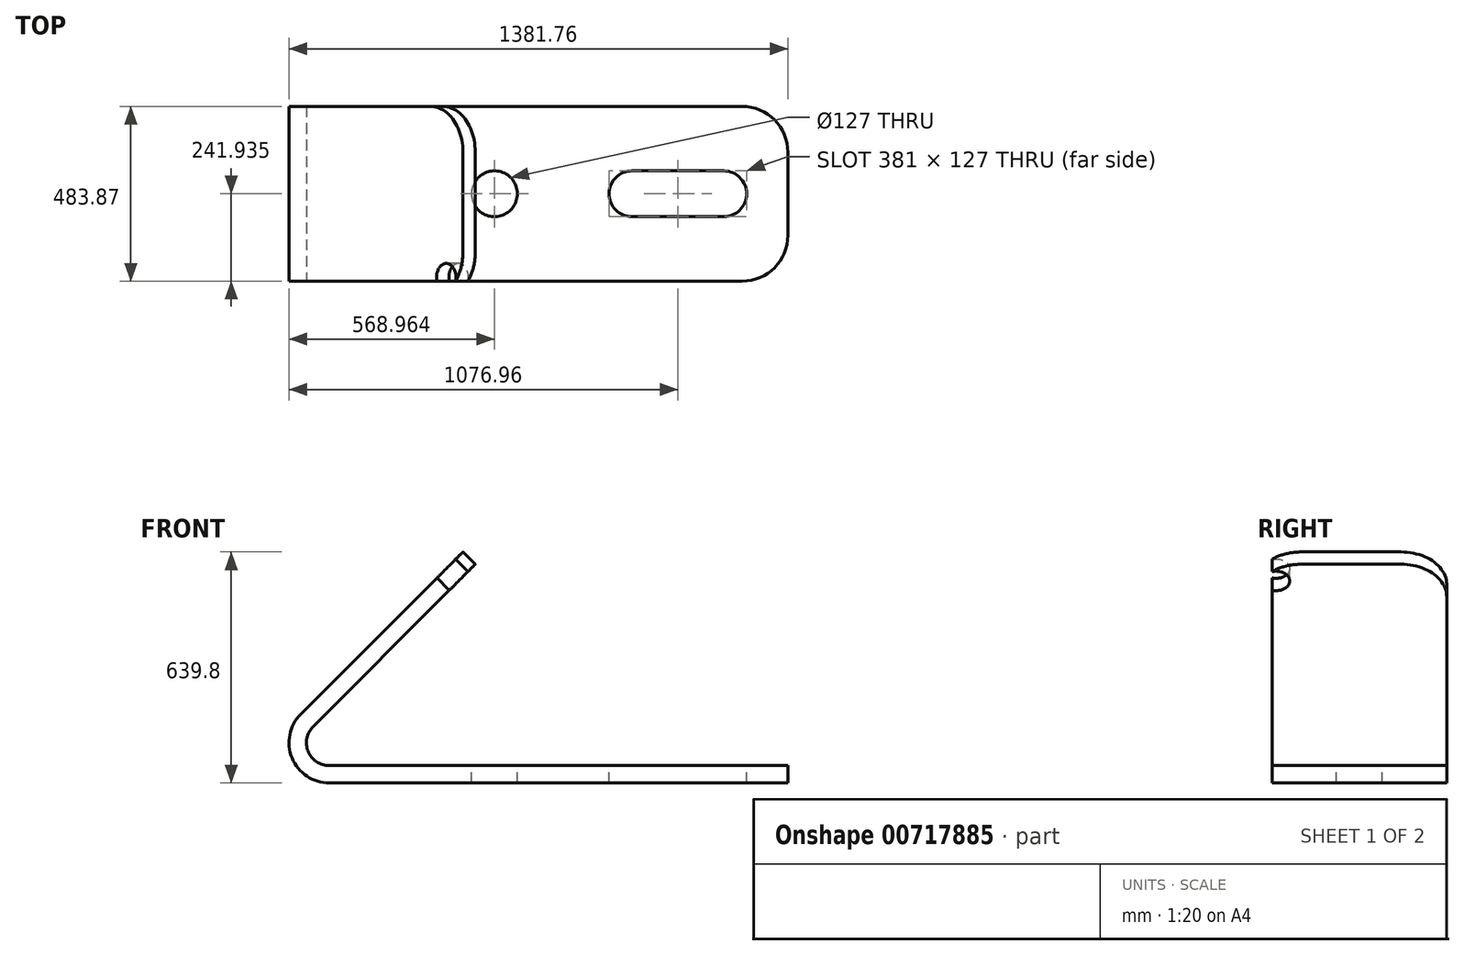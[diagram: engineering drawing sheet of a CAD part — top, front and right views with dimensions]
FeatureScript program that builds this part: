
annotation { "Feature Type Name" : "Feature", "Feature Type Description" : "" }
export const myFeature = defineFeature(function(context is Context, id is Id, definition is map)
    precondition{}
    {
        {
            var Q0;
            Q0=qCreatedBy(makeId("Front.planeOp"),FACE);
            var sketch = newSketch(context, id + "F0", { "sketchPlane" : qUnion([Q0])});
            skLineSegment(sketch, "E0", {"start": v(-755.86, 0) * mm, "end": v(514.14, 0) * mm});
            skLineSegment(sketch, "E1", {"start": v(514.14, 48.26) * mm, "end": v(-755.86, 48.26) * mm});
            skLineSegment(sketch, "E2", {"start": v(514.14, 48.26) * mm, "end": v(514.14, 0) * mm});
            skArc(sketch, "E3", {"start": v(-834.88, 190.79) * mm, "mid": v(-859.1, 69) * mm, "end": v(-755.86, 0) * mm});
            skCircle(sketch, "E4", {"center": v(-755.86, 111.76) * mm, "radius": 63.5 * mm});
            skLineSegment(sketch, "E5", {"start": v(-834.88, 190.79) * mm, "end": v(-385.87, 639.8) * mm});
            skLineSegment(sketch, "E6", {"start": v(-385.87, 639.8) * mm, "end": v(-351.74, 605.67) * mm});
            skLineSegment(sketch, "E7", {"start": v(-351.74, 605.67) * mm, "end": v(-800.76, 156.66) * mm});
            skSolve(sketch);
        }
        {
            var Q0;
            Q0=makeQuery(id+"F0.imprint","IMPRINT",FACE,{"disambiguationData":[TD([[makeQuery(id+"F0.imprint","IMPRINT",EDGE,{"derivedFrom":sQuery(id+"F0.wireOp",EDGE,"E0")}),1.0]])]});
            extrude(context, id + "F1", {"entities" : qUnion([Q0]), "oppositeDirection" : true, "depth" : 483.87 * mm, "offsetDistance" : 25.4 * mm});
        }
        {
            var Q0;
            Q0=makeQuery(id+"F1.opExtrude","SWEPT_FACE",FACE,{"disambiguationData":[OSD([sQuery(id+"F0.wireOp",EDGE,"E1")])]});
            var sketch = newSketch(context, id + "F2", { "sketchPlane" : qUnion([Q0])});
            skLineSegment(sketch, "E8", {"start": v(514.14, 483.87) * mm, "end": v(-298.66, 483.87) * mm, "construction": true});
            skLineSegment(sketch, "E9", {"start": v(-298.66, 483.87) * mm, "end": v(-298.66, 241.94) * mm, "construction": true});
            skCircle(sketch, "E10", {"center": v(-298.66, 241.94) * mm, "radius": 63.5 * mm});
            skLineSegment(sketch, "E11", {"start": v(18.84, 241.94) * mm, "end": v(399.84, 241.94) * mm, "construction": true});
            skLineSegment(sketch, "E12", {"start": v(82.34, 305.44) * mm, "end": v(336.34, 305.44) * mm});
            skLineSegment(sketch, "E13.MirrorCS", {"start": v(82.34, 178.44) * mm, "end": v(336.34, 178.44) * mm});
            skArc(sketch, "E14", {"start": v(82.34, 305.44) * mm, "mid": v(18.84, 241.93) * mm, "end": v(82.34, 178.43) * mm});
            skArc(sketch, "E15", {"start": v(336.34, 178.44) * mm, "mid": v(399.84, 241.94) * mm, "end": v(336.34, 305.44) * mm});
            skPoint(sketch, "E16.MirrorCS.end.orphan", {"position": v(399.84, 241.94) * mm});
            skPoint(sketch, "E16.MirrorCS.start.orphan", {"position": v(399.84, 178.44) * mm});
            skPoint(sketch, "E17.MirrorCS.end.orphan", {"position": v(18.84, 178.44) * mm});
            skPoint(sketch, "E17.MirrorCS.start.orphan", {"position": v(18.84, 241.94) * mm});
            skSolve(sketch);
        }
        {
            var Q0;
            Q0=makeQuery(id+"F2.imprint","IMPRINT",FACE,{"disambiguationData":[TD([[makeQuery(id+"F2.imprint","IMPRINT",EDGE,{"derivedFrom":sQuery(id+"F2.wireOp",EDGE,"E12")}),-1.0]])]});
            var Q1;
            Q1=makeQuery(id+"F2.imprint","IMPRINT",FACE,{"disambiguationData":[TD([[makeQuery(id+"F2.imprint","IMPRINT",EDGE,{"derivedFrom":sQuery(id+"F2.wireOp",EDGE,"E10")}),1.0]])]});
            extrude(context, id + "F3", {"entities" : qUnion([Q0, Q1]), "operationType" : NewBodyOperationType.REMOVE, "oppositeDirection" : true, "depth" : 83.82 * mm, "offsetDistance" : 25.4 * mm});
        }
        {
            var Q0;
            Q0=makeQuery(id+"F1.opExtrude","SWEPT_FACE",FACE,{"disambiguationData":[OSD([sQuery(id+"F0.wireOp",EDGE,"E5")])]});
            var sketch = newSketch(context, id + "F4", { "sketchPlane" : qUnion([Q0])});
            skLineSegment(sketch, "E18", {"start": v(179.56, 0) * mm, "end": v(-10.94, 0) * mm, "construction": true});
            skLineSegment(sketch, "E19", {"start": v(-10.94, 0) * mm, "end": v(-10.94, 114.3) * mm, "construction": true});
            skCircle(sketch, "E20", {"center": v(-10.94, 114.3) * mm, "radius": 38.1 * mm});
            skLineSegment(sketch, "E21", {"start": v(179.56, 241.94) * mm, "end": v(-455.44, 241.94) * mm, "construction": true});
            skCircle(sketch, "E22.MirrorC", {"center": v(-10.94, 369.57) * mm, "radius": 38.1 * mm});
            skSolve(sketch);
        }
        {
            var Q0;
            Q0=makeQuery(id+"F4.imprint","IMPRINT",FACE,{"disambiguationData":[TD([[makeQuery(id+"F4.imprint","IMPRINT",EDGE,{"derivedFrom":sQuery(id+"F4.wireOp",EDGE,"E22.MirrorC")}),-1.0]])]});
            var Q1;
            Q1=makeQuery(id+"F4.imprint","IMPRINT",FACE,{"disambiguationData":[TD([[makeQuery(id+"F4.imprint","IMPRINT",EDGE,{"derivedFrom":sQuery(id+"F4.wireOp",EDGE,"E20")}),1.0]])]});
            extrude(context, id + "F5", {"entities" : qUnion([Q0, Q1]), "operationType" : NewBodyOperationType.REMOVE, "oppositeDirection" : true, "depth" : 101.6 * mm, "offsetDistance" : 25.4 * mm});
        }
        {
            var Q0;
            Q0=makeQuery(id+"F1.opExtrude","CAP_EDGE",EDGE,{"disambiguationData":[OSD([sQuery(id+"F0.wireOp",EDGE,"E6")])],"isStart":false});
            var Q1;
            Q1=makeQuery(id+"F1.opExtrude","CAP_EDGE",EDGE,{"disambiguationData":[OSD([sQuery(id+"F0.wireOp",EDGE,"E6")])],"isStart":true});
            var Q2;
            Q2=makeQuery(id+"F1.opExtrude","CAP_EDGE",EDGE,{"disambiguationData":[OSD([sQuery(id+"F0.wireOp",EDGE,"E2")])],"isStart":false});
            var Q3;
            Q3=makeQuery(id+"F1.opExtrude","CAP_EDGE",EDGE,{"disambiguationData":[OSD([sQuery(id+"F0.wireOp",EDGE,"E2")])],"isStart":true});
            fillet(context, id + "F6", {"entities" : qUnion([Q0, Q1, Q2, Q3]), "radius" : 127 * mm, "tangentPropagation" : true, "allowEdgeOverflow" : false});
        }
    });
